# Revit family: EDF15R
name_source: partatom
category: Plumbing Fixtures
units: mm (PartAtom-declared; Revit-internal decimal feet)

## family parameters
Always vertical = Yes
Cut with Voids When Loaded = No
OmniClass Number = 23.45.00.00
OmniClass Title = Sanitary, Laundry, and Cleaning Equipment
Part Type = Normal
Room Calculation Point = No
Round Connector Dimension = Use Diameter
Shared = No
Work Plane-Based = No

## types (1)
- White Granite Composite (WHT)
    Activation by = Mechanical Top Bubbler Button
    Approx. Shipping Weight = 5 lbs.
    Assembly Code = D2010810
    BODY_MATERIAL = WHT-White Granite Composite
    BUBBLER_MATERIAL = Metal - Steel - Stainless - Chrome
    BUTTON_MATERIAL = Metal - Steel - Stainless - Chrome
    Bubbler Style = Push Button
    CW Connection = Yes
    Chilling Option = Non-refrigerated
    DRAIN_MATERIAL = Metal - Steel - Stainless - Chrome
    Description = Halsey Taylor Bracket Fountain
Non-Filtered Non-Refrigerated Stainless
    Dimensions (L x W x H) = 10inch x 11inch x 4 7/8Inch
    Drain_Pipe 1 1/2" = 25 mm  [stored 0.082021 ft]
    Finish = Stainless Steel
    HW Connection = No
    Inlet_Pipe = 10 mm  [stored 0.0328084 ft]
    Installation Location = Indoor +Outdoor
    Manufacturer = Elkay
    Model = EDF15R
    Mounting Type = Wall Mount (On Wall)
    No. of Stations Served = 1
    Order ID = 74025015001
    Power = No Electrical Required
    SINK_MATERIAL = Metal - Steel - Stainless - Chrome
    Vent Connection = No
    Version = 1.0.0.0
    Waste Connection = Yes

note: [stored X ft] marks values corroborated as IEEE doubles in the binary element streams (Revit-internal decimal feet)

## geometry (parser evidence)
native form markers: Sweep x15
no freeform markers — native parametric forms only
